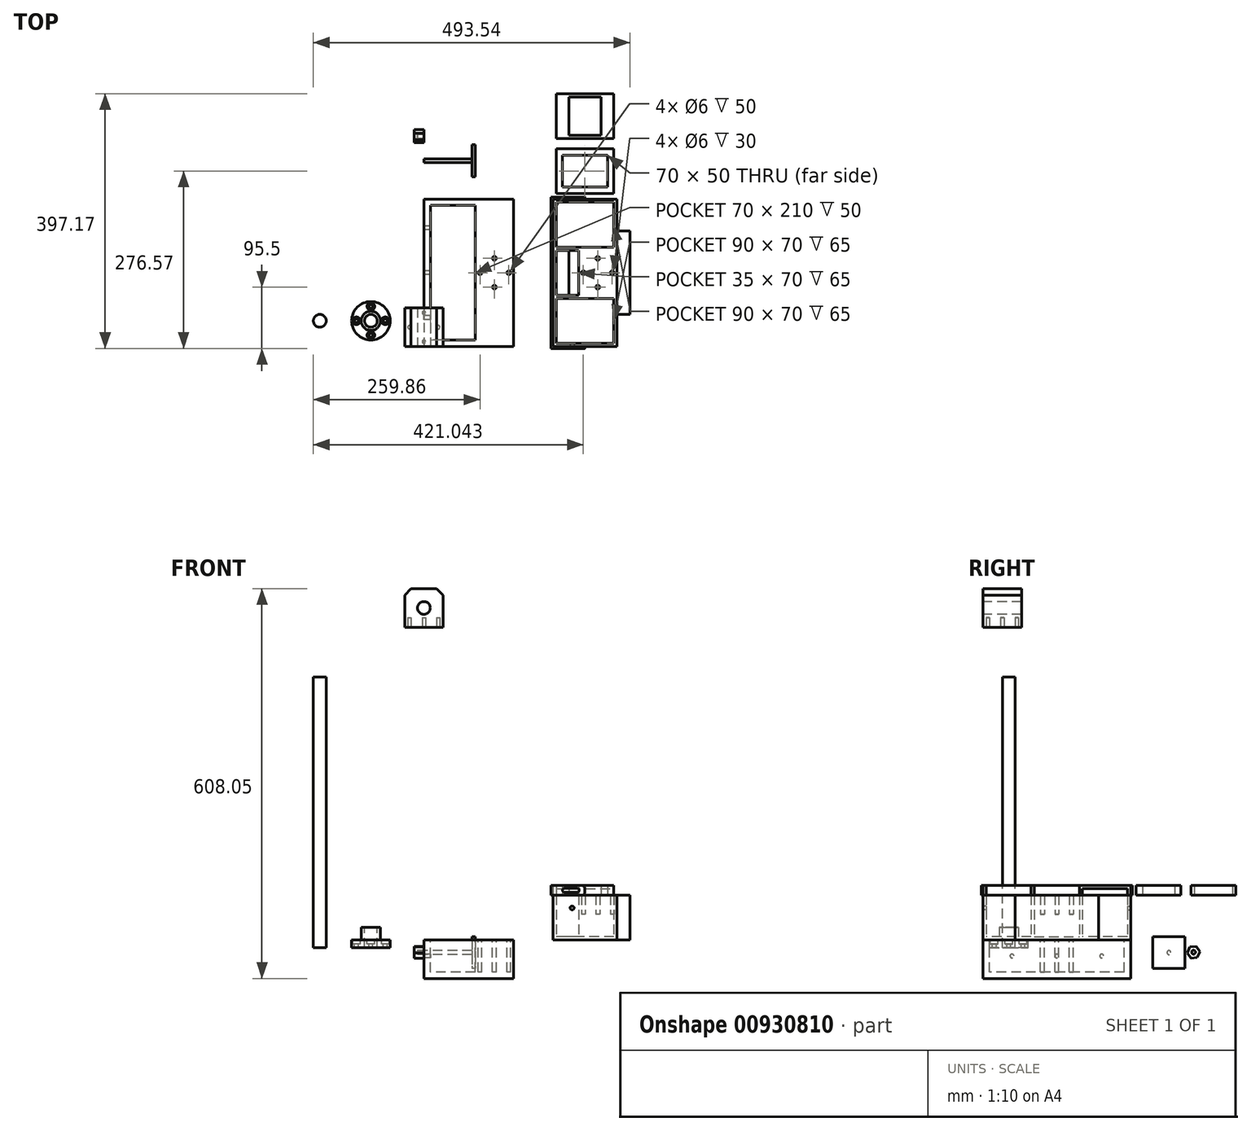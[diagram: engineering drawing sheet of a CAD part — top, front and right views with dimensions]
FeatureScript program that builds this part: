
annotation { "Feature Type Name" : "Feature", "Feature Type Description" : "" }
export const myFeature = defineFeature(function(context is Context, id is Id, definition is map)
    precondition{}
    {
        {
            var Q0;
            Q0=qCreatedBy(makeId("Front.planeOp"),FACE);
            var sketch = newSketch(context, id + "F0", { "sketchPlane" : qUnion([Q0])});
            skLineSegment(sketch, "E0.bottom", {"start": v(0, -100) * mm, "end": v(140, -100) * mm});
            skLineSegment(sketch, "E0.top", {"start": v(0, -160) * mm, "end": v(140, -160) * mm});
            skLineSegment(sketch, "E0.left", {"start": v(0, -100) * mm, "end": v(0, -160) * mm});
            skLineSegment(sketch, "E0.right", {"start": v(140, -100) * mm, "end": v(140, -160) * mm});
            skSolve(sketch);
        }
        {
            var Q0;
            Q0=qSketchRegion(id+"F0",true);
            extrude(context, id + "F1", {"entities" : qUnion([Q0]), "oppositeDirection" : true, "depth" : 230 * mm, "offsetDistance" : 25 * mm});
        }
        {
            var Q0;
            Q0=makeQuery(id+"F1.opExtrude","SWEPT_FACE",FACE,{"disambiguationData":[OSD([sQuery(id+"F0.wireOp",EDGE,"E0.bottom")])]});
            var sketch = newSketch(context, id + "F2", { "sketchPlane" : qUnion([Q0])});
            skCircle(sketch, "E1", {"center": v(-82.66, 40) * mm, "radius": 30 * mm});
            skCircle(sketch, "E2", {"center": v(-82.66, 40) * mm, "radius": 10 * mm});
            skCircle(sketch, "E3", {"center": v(-82.66, 40) * mm, "radius": 15 * mm});
            skCircle(sketch, "E4", {"center": v(-82.66, 62.5) * mm, "radius": 3 * mm});
            skCircle(sketch, "E5.1.0", {"center": v(-105.16, 40) * mm, "radius": 3 * mm});
            skCircle(sketch, "E5.2.0", {"center": v(-82.66, 17.5) * mm, "radius": 3 * mm});
            skCircle(sketch, "E5.3.0", {"center": v(-60.16, 40) * mm, "radius": 3 * mm});
            skCircle(sketch, "E6", {"center": v(-82.66, 62.5) * mm, "radius": 6 * mm});
            skCircle(sketch, "E7", {"center": v(-60.16, 40) * mm, "radius": 6 * mm});
            skCircle(sketch, "E8", {"center": v(-82.66, 17.5) * mm, "radius": 6 * mm});
            skCircle(sketch, "E9", {"center": v(-105.16, 40) * mm, "radius": 6 * mm});
            skCircle(sketch, "E10", {"center": v(-162.36, 40) * mm, "radius": 10 * mm});
            skSolve(sketch);
        }
        {
            var Q0;
            Q0=makeQuery(id+"F2.imprint","IMPRINT",FACE,{"disambiguationData":[TD([[makeQuery(id+"F2.imprint","IMPRINT",EDGE,{"derivedFrom":sQuery(id+"F2.wireOp",EDGE,"E1")}),1.0]])]});
            var Q1;
            Q1=makeQuery(id+"F2.imprint","IMPRINT",FACE,{"disambiguationData":[TD([[makeQuery(id+"F2.imprint","IMPRINT",EDGE,{"derivedFrom":sQuery(id+"F2.wireOp",EDGE,"E5.1.0")}),-1.0]])]});
            var Q2;
            Q2=makeQuery(id+"F2.imprint","IMPRINT",FACE,{"disambiguationData":[TD([[makeQuery(id+"F2.imprint","IMPRINT",EDGE,{"derivedFrom":sQuery(id+"F2.wireOp",EDGE,"E2")}),-1.0]])]});
            var Q3;
            Q3=makeQuery(id+"F2.imprint","IMPRINT",FACE,{"disambiguationData":[TD([[makeQuery(id+"F2.imprint","IMPRINT",EDGE,{"derivedFrom":sQuery(id+"F2.wireOp",EDGE,"E4")}),-1.0]])]});
            var Q4;
            Q4=makeQuery(id+"F2.imprint","IMPRINT",FACE,{"disambiguationData":[TD([[makeQuery(id+"F2.imprint","IMPRINT",EDGE,{"derivedFrom":sQuery(id+"F2.wireOp",EDGE,"E5.3.0")}),-1.0]])]});
            var Q5;
            Q5=makeQuery(id+"F2.imprint","IMPRINT",FACE,{"disambiguationData":[TD([[makeQuery(id+"F2.imprint","IMPRINT",EDGE,{"derivedFrom":sQuery(id+"F2.wireOp",EDGE,"E5.2.0")}),-1.0]])]});
            var Q6;
            Q6=makeQuery(id+"F2.imprint","IMPRINT",FACE,{"disambiguationData":[TD([[makeQuery(id+"F2.imprint","IMPRINT",EDGE,{"derivedFrom":sQuery(id+"F2.wireOp",EDGE,"E1")}),1.0]])]});
            var Q7;
            Q7=makeQuery(id+"F2.imprint","IMPRINT",FACE,{"disambiguationData":[TD([[makeQuery(id+"F2.imprint","IMPRINT",EDGE,{"derivedFrom":sQuery(id+"F2.wireOp",EDGE,"E10")}),1.0]])]});
            extrude(context, id + "F3", {"entities" : qUnion([Q0, Q1, Q2, Q3, Q4, Q5, Q6, Q7]), "oppositeDirection" : true, "depth" : 12 * mm, "offsetDistance" : 25 * mm});
        }
        {
            var Q0;
            Q0=makeQuery(id+"F2.imprint","IMPRINT",FACE,{"disambiguationData":[TD([[makeQuery(id+"F2.imprint","IMPRINT",EDGE,{"derivedFrom":sQuery(id+"F2.wireOp",EDGE,"E4")}),-1.0]])]});
            var Q1;
            Q1=makeQuery(id+"F2.imprint","IMPRINT",FACE,{"disambiguationData":[TD([[makeQuery(id+"F2.imprint","IMPRINT",EDGE,{"derivedFrom":sQuery(id+"F2.wireOp",EDGE,"E5.3.0")}),-1.0]])]});
            var Q2;
            Q2=makeQuery(id+"F2.imprint","IMPRINT",FACE,{"disambiguationData":[TD([[makeQuery(id+"F2.imprint","IMPRINT",EDGE,{"derivedFrom":sQuery(id+"F2.wireOp",EDGE,"E5.2.0")}),-1.0]])]});
            var Q3;
            Q3=makeQuery(id+"F2.imprint","IMPRINT",FACE,{"disambiguationData":[TD([[makeQuery(id+"F2.imprint","IMPRINT",EDGE,{"derivedFrom":sQuery(id+"F2.wireOp",EDGE,"E5.1.0")}),-1.0]])]});
            extrude(context, id + "F4", {"entities" : qUnion([Q0, Q1, Q2, Q3]), "operationType" : NewBodyOperationType.REMOVE, "oppositeDirection" : true, "depth" : 6 * mm, "offsetDistance" : 25 * mm});
        }
        {
            var Q0;
            Q0=makeQuery(id+"F2.imprint","IMPRINT",FACE,{"disambiguationData":[TD([[makeQuery(id+"F2.imprint","IMPRINT",EDGE,{"derivedFrom":sQuery(id+"F2.wireOp",EDGE,"E2")}),-1.0]])]});
            extrude(context, id + "F5", {"entities" : qUnion([Q0]), "operationType" : NewBodyOperationType.ADD, "depth" : 20 * mm, "offsetDistance" : 25 * mm});
        }
        {
            var Q0;
            Q0=makeQuery(id+"F2.imprint","IMPRINT",FACE,{"disambiguationData":[TD([[makeQuery(id+"F2.imprint","IMPRINT",EDGE,{"derivedFrom":sQuery(id+"F2.wireOp",EDGE,"E10")}),1.0]])]});
            extrude(context, id + "F6", {"entities" : qUnion([Q0]), "operationType" : NewBodyOperationType.ADD, "depth" : 410 * mm, "offsetDistance" : 25 * mm});
        }
        {
            var Q0;
            Q0=qCreatedBy(makeId("Front.planeOp"),FACE);
            var sketch = newSketch(context, id + "F7", { "sketchPlane" : qUnion([Q0])});
            skLineSegment(sketch, "E11.top", {"start": v(-30, 388.05) * mm, "end": v(30, 388.05) * mm});
            skLineSegment(sketch, "E11.left", {"start": v(-30, 448.05) * mm, "end": v(-30, 388.05) * mm});
            skLineSegment(sketch, "E11.right", {"start": v(30, 448.05) * mm, "end": v(30, 388.05) * mm});
            skPoint(sketch, "E11.middle", {"position": v(0, 418.05) * mm});
            skCircle(sketch, "E12", {"center": v(0, 418.05) * mm, "radius": 10 * mm});
            skLineSegment(sketch, "E13", {"start": v(30, 448.05) * mm, "end": v(-30, 448.05) * mm});
            skSolve(sketch);
        }
        {
            var Q0;
            Q0=qSketchRegion(id+"F7",true);
            extrude(context, id + "F8", {"entities" : qUnion([Q0]), "oppositeDirection" : true, "depth" : 60 * mm, "offsetDistance" : 25 * mm});
        }
        {
            var Q0;
            Q0=makeQuery(id+"F8.opExtrude","SWEPT_FACE",FACE,{"disambiguationData":[OSD([sQuery(id+"F7.wireOp",EDGE,"E11.top")])]});
            var sketch = newSketch(context, id + "F9", { "sketchPlane" : qUnion([Q0])});
            skCircle(sketch, "E14", {"center": v(0, -7.5) * mm, "radius": 2.6 * mm});
            skCircle(sketch, "E15.1.0", {"center": v(-22.5, -30) * mm, "radius": 2.6 * mm});
            skCircle(sketch, "E15.2.0", {"center": v(0, -52.5) * mm, "radius": 2.6 * mm});
            skCircle(sketch, "E15.3.0", {"center": v(22.5, -30) * mm, "radius": 2.6 * mm});
            skPoint(sketch, "E15.center", {"position": v(0, -30) * mm});
            skSolve(sketch);
        }
        {
            var Q0;
            Q0=qSketchRegion(id+"F9",true);
            extrude(context, id + "F10", {"entities" : qUnion([Q0]), "operationType" : NewBodyOperationType.REMOVE, "oppositeDirection" : true, "depth" : 15 * mm, "offsetDistance" : 25 * mm});
        }
        {
            var Q0;
            {var subQ0=sQuery(id+"F0.wireOp",EDGE,"E0.bottom");Q0=makeQuery(id+"F2.imprint","IMPRINT",FACE,{"disambiguationData":[TD([[makeQuery(id+"F2.imprint","IMPRINT",EDGE,{"derivedFrom":makeQuery(id+"F1.opExtrude","CAP_EDGE",EDGE,{"disambiguationData":[OSD([subQ0])],"isStart":true})}),1.0]])]});}
            var sketch = newSketch(context, id + "F11", { "sketchPlane" : qUnion([Q0])});
            skLineSegment(sketch, "E16.bottom", {"start": v(80, 220) * mm, "end": v(10, 220) * mm});
            skLineSegment(sketch, "E16.top", {"start": v(80, 10) * mm, "end": v(10, 10) * mm});
            skLineSegment(sketch, "E16.left", {"start": v(80, 220) * mm, "end": v(80, 10) * mm});
            skLineSegment(sketch, "E16.right", {"start": v(10, 220) * mm, "end": v(10, 10) * mm});
            skCircle(sketch, "E17", {"center": v(110, 137.5) * mm, "radius": 3 * mm});
            skCircle(sketch, "E18.1.0", {"center": v(87.5, 115) * mm, "radius": 3 * mm});
            skCircle(sketch, "E18.2.0", {"center": v(110, 92.5) * mm, "radius": 3 * mm});
            skPoint(sketch, "E18.center", {"position": v(110, 115) * mm});
            skCircle(sketch, "E19.1.3.0", {"center": v(132.5, 115) * mm, "radius": 3 * mm});
            skSolve(sketch);
        }
        {
            var Q0;
            Q0 = qSketchRegion(id + "F11", true);
            extrude(context, id + "F12", {"entities" : qUnion([Q0]), "operationType" : NewBodyOperationType.REMOVE, "oppositeDirection" : true, "depth" : 50 * mm, "offsetDistance" : 25 * mm});
        }
        {
            var Q0;
            Q0=makeQuery(id+"F1.opExtrude","SWEPT_FACE",FACE,{"disambiguationData":[OSD([sQuery(id+"F0.wireOp",EDGE,"E0.left")])]});
            var sketch = newSketch(context, id + "F13", { "sketchPlane" : qUnion([Q0])});
            skCircle(sketch, "E20", {"center": v(-115, -125) * mm, "radius": 3 * mm});
            skCircle(sketch, "E21", {"center": v(-185, -125) * mm, "radius": 3 * mm});
            skCircle(sketch, "E22.MirrorC", {"center": v(-45, -125) * mm, "radius": 3 * mm});
            skSolve(sketch);
        }
        {
            var Q0;
            Q0 = qSketchRegion(id + "F13", true);
            extrude(context, id + "F14", {"entities" : qUnion([Q0]), "operationType" : NewBodyOperationType.REMOVE, "oppositeDirection" : true, "depth" : 10 * mm, "offsetDistance" : 25 * mm});
        }
        {
            var Q0;
            Q0=makeQuery(id+"F1.opExtrude","SWEPT_FACE",FACE,{"disambiguationData":[OSD([sQuery(id+"F0.wireOp",EDGE,"E0.left")])]});
            var sketch = newSketch(context, id + "F15", { "sketchPlane" : qUnion([Q0])});
            skLineSegment(sketch, "E23.bottom", {"start": v(-314.84, -94.64) * mm, "end": v(-264.84, -94.64) * mm});
            skLineSegment(sketch, "E23.top", {"start": v(-314.84, -144.64) * mm, "end": v(-264.84, -144.64) * mm});
            skLineSegment(sketch, "E23.left", {"start": v(-314.84, -94.64) * mm, "end": v(-314.84, -144.64) * mm});
            skLineSegment(sketch, "E23.right", {"start": v(-264.84, -94.64) * mm, "end": v(-264.84, -144.64) * mm});
            skPoint(sketch, "E23.middle", {"position": v(-289.84, -119.64) * mm});
            skCircle(sketch, "E24", {"center": v(-289.84, -119.64) * mm, "radius": 3 * mm});
            skSolve(sketch);
        }
        {
            var Q0;
            Q0=makeQuery(id+"F1.opExtrude","SWEPT_FACE",FACE,{"disambiguationData":[OSD([sQuery(id+"F0.wireOp",EDGE,"E0.left")])]});
            var sketch = newSketch(context, id + "F16", { "sketchPlane" : qUnion([Q0])});
            skCircle(sketch, "E25", {"center": v(-328.25, -119.07) * mm, "radius": 3 * mm});
            skCircle(sketch, "E26.cCircle", {"center": v(-328.25, -119.07) * mm, "radius": 10 * mm, "construction": true});
            skLineSegment(sketch, "E26.0", {"start": v(-322.4, -110.95) * mm, "end": v(-318.3, -120.07) * mm});
            skLineSegment(sketch, "E26.1", {"start": v(-318.3, -120.07) * mm, "end": v(-324.15, -128.18) * mm});
            skLineSegment(sketch, "E26.2", {"start": v(-324.15, -128.18) * mm, "end": v(-334.1, -127.18) * mm});
            skLineSegment(sketch, "E26.3", {"start": v(-334.1, -127.18) * mm, "end": v(-338.2, -118.06) * mm});
            skLineSegment(sketch, "E26.4", {"start": v(-338.2, -118.06) * mm, "end": v(-332.36, -109.95) * mm});
            skLineSegment(sketch, "E26.5", {"start": v(-332.36, -109.95) * mm, "end": v(-322.4, -110.95) * mm});
            skSolve(sketch);
        }
        {
            var Q0;
            Q0=makeQuery(id+"F16.imprint","IMPRINT",FACE,{"disambiguationData":[TD([[makeQuery(id+"F16.imprint","IMPRINT",EDGE,{"derivedFrom":sQuery(id+"F16.wireOp",EDGE,"E25")}),-1.0]])]});
            var Q1;
            Q1=makeQuery(id+"F16.imprint","IMPRINT",FACE,{"disambiguationData":[TD([[makeQuery(id+"F16.imprint","IMPRINT",EDGE,{"derivedFrom":sQuery(id+"F16.wireOp",EDGE,"E25")}),1.0]])]});
            extrude(context, id + "F17", {"entities" : qUnion([Q0, Q1]), "depth" : 15 * mm, "offsetDistance" : 25 * mm});
        }
        {
            var Q0;
            Q0=makeQuery(id+"F16.imprint","IMPRINT",FACE,{"disambiguationData":[TD([[makeQuery(id+"F16.imprint","IMPRINT",EDGE,{"derivedFrom":sQuery(id+"F16.wireOp",EDGE,"E25")}),1.0]])]});
            extrude(context, id + "F18", {"entities" : qUnion([Q0]), "operationType" : NewBodyOperationType.REMOVE, "depth" : 10 * mm, "offsetDistance" : 25 * mm});
        }
        {
            var Q0;
            Q0=makeQuery(id+"F15.imprint","IMPRINT",FACE,{"disambiguationData":[TD([[makeQuery(id+"F15.imprint","IMPRINT",EDGE,{"derivedFrom":sQuery(id+"F15.wireOp",EDGE,"E23.bottom")}),-1.0]])]});
            var Q1;
            Q1=makeQuery(id+"F15.imprint","IMPRINT",FACE,{"disambiguationData":[TD([[makeQuery(id+"F15.imprint","IMPRINT",EDGE,{"derivedFrom":sQuery(id+"F15.wireOp",EDGE,"E24")}),1.0]])]});
            extrude(context, id + "F19", {"entities" : qUnion([Q0, Q1]), "oppositeDirection" : true, "depth" : 80 * mm, "offsetDistance" : 25 * mm});
        }
        {
            var Q0;
            Q0 = qSketchRegion(id + "F15", true);
            extrude(context, id + "F20", {"entities" : qUnion([Q0]), "operationType" : NewBodyOperationType.REMOVE, "oppositeDirection" : true, "depth" : 75 * mm, "offsetDistance" : 25 * mm});
        }
        {
            var Q0;
            Q0=makeQuery(id+"F8.opExtrude","SWEPT_EDGE",EDGE,{"disambiguationData":[OSD([sQuery(id+"F7.wireOp",EDGE,"E11.left"),sQuery(id+"F7.wireOp",EDGE,"E13")])]});
            var Q1;
            Q1=makeQuery(id+"F8.opExtrude","SWEPT_EDGE",EDGE,{"disambiguationData":[OSD([sQuery(id+"F7.wireOp",EDGE,"E11.right"),sQuery(id+"F7.wireOp",EDGE,"E13")])]});
            chamfer(context, id + "F21", {"entities" : qUnion([Q0, Q1]), "width" : 10 * mm, "tangentPropagation" : true});
        }
        {
            var Q0;
            {var subQ0=sQuery(id+"F0.wireOp",EDGE,"E0.bottom");Q0=makeQuery(id+"F2.imprint","IMPRINT",FACE,{"disambiguationData":[TD([[makeQuery(id+"F2.imprint","IMPRINT",EDGE,{"derivedFrom":makeQuery(id+"F1.opExtrude","CAP_EDGE",EDGE,{"disambiguationData":[OSD([subQ0])],"isStart":true})}),1.0]])]});}
            var sketch = newSketch(context, id + "F22", { "sketchPlane" : qUnion([Q0])});
            skLineSegment(sketch, "E27.bottom", {"start": v(201.18, 0) * mm, "end": v(301.18, 0) * mm});
            skLineSegment(sketch, "E27.top", {"start": v(201.18, 230) * mm, "end": v(301.18, 230) * mm});
            skLineSegment(sketch, "E27.left", {"start": v(201.18, 0) * mm, "end": v(201.18, 230) * mm});
            skLineSegment(sketch, "E27.right", {"start": v(301.18, 0) * mm, "end": v(301.18, 230) * mm});
            skLineSegment(sketch, "E28.0", {"start": v(206.18, 225) * mm, "end": v(296.18, 225) * mm});
            skLineSegment(sketch, "E28.1", {"start": v(206.18, 5) * mm, "end": v(206.18, 75) * mm});
            skLineSegment(sketch, "E28.2", {"start": v(206.18, 5) * mm, "end": v(296.18, 5) * mm});
            skLineSegment(sketch, "E28.3", {"start": v(296.18, 5) * mm, "end": v(296.18, 75) * mm});
            skLineSegment(sketch, "E29", {"start": v(206.18, 75) * mm, "end": v(296.18, 75) * mm});
            skLineSegment(sketch, "E30", {"start": v(206.18, 155) * mm, "end": v(296.18, 155) * mm});
            skLineSegment(sketch, "E31.trimOffspring", {"start": v(206.18, 155) * mm, "end": v(206.18, 225) * mm});
            skLineSegment(sketch, "E32.trimOffspring", {"start": v(296.18, 155) * mm, "end": v(296.18, 225) * mm});
            skCircle(sketch, "E33", {"center": v(271.18, 137.5) * mm, "radius": 3 * mm});
            skCircle(sketch, "E34", {"center": v(271.18, 92.5) * mm, "radius": 3 * mm});
            skCircle(sketch, "E35", {"center": v(293.68, 115) * mm, "radius": 3 * mm});
            skCircle(sketch, "E36", {"center": v(248.68, 115) * mm, "radius": 3 * mm});
            skLineSegment(sketch, "E37.bottom", {"start": v(206.18, 150) * mm, "end": v(241.18, 150) * mm});
            skLineSegment(sketch, "E37.top", {"start": v(206.18, 80) * mm, "end": v(241.18, 80) * mm});
            skLineSegment(sketch, "E37.left", {"start": v(206.18, 150) * mm, "end": v(206.18, 80) * mm});
            skLineSegment(sketch, "E37.right", {"start": v(241.18, 150) * mm, "end": v(241.18, 80) * mm});
            skSolve(sketch);
        }
        {
            var Q0;
            Q0=makeQuery(id+"F22.imprint","IMPRINT",FACE,{"disambiguationData":[TD([[makeQuery(id+"F22.imprint","IMPRINT",EDGE,{"derivedFrom":sQuery(id+"F22.wireOp",EDGE,"E27.bottom")}),1.0]])]});
            var Q1;
            Q1=makeQuery(id+"F22.imprint","IMPRINT",FACE,{"disambiguationData":[TD([[makeQuery(id+"F22.imprint","IMPRINT",EDGE,{"derivedFrom":sQuery(id+"F22.wireOp",EDGE,"E34")}),1.0]])]});
            var Q2;
            Q2=makeQuery(id+"F22.imprint","IMPRINT",FACE,{"disambiguationData":[TD([[makeQuery(id+"F22.imprint","IMPRINT",EDGE,{"derivedFrom":sQuery(id+"F22.wireOp",EDGE,"E36")}),1.0]])]});
            var Q3;
            Q3=makeQuery(id+"F22.imprint","IMPRINT",FACE,{"disambiguationData":[TD([[makeQuery(id+"F22.imprint","IMPRINT",EDGE,{"derivedFrom":sQuery(id+"F22.wireOp",EDGE,"E35")}),1.0]])]});
            var Q4;
            Q4=makeQuery(id+"F22.imprint","IMPRINT",FACE,{"disambiguationData":[TD([[makeQuery(id+"F22.imprint","IMPRINT",EDGE,{"derivedFrom":sQuery(id+"F22.wireOp",EDGE,"E33")}),1.0]])]});
            var Q5;
            Q5=makeQuery(id+"F22.imprint","IMPRINT",FACE,{"disambiguationData":[TD([[makeQuery(id+"F22.imprint","IMPRINT",EDGE,{"derivedFrom":sQuery(id+"F22.wireOp",EDGE,"E37.bottom")}),-1.0]])]});
            var Q6;
            Q6=makeQuery(id+"F22.imprint","IMPRINT",FACE,{"disambiguationData":[TD([[makeQuery(id+"F22.imprint","IMPRINT",EDGE,{"derivedFrom":sQuery(id+"F22.wireOp",EDGE,"E28.1")}),-1.0]])]});
            var Q7;
            Q7=makeQuery(id+"F22.imprint","IMPRINT",FACE,{"disambiguationData":[TD([[makeQuery(id+"F22.imprint","IMPRINT",EDGE,{"derivedFrom":sQuery(id+"F22.wireOp",EDGE,"E28.0")}),-1.0]])]});
            extrude(context, id + "F23", {"entities" : qUnion([Q0, Q1, Q2, Q3, Q4, Q5, Q6, Q7]), "depth" : 5 * mm, "offsetDistance" : 25 * mm});
        }
        {
            var Q0;
            Q0 = qSketchRegion(id + "F22", true);
            extrude(context, id + "F24", {"entities" : qUnion([Q0]), "operationType" : NewBodyOperationType.ADD, "depth" : 70 * mm, "offsetDistance" : 25 * mm});
        }
        {
            var Q0;
            Q0=makeQuery(id+"F22.imprint","IMPRINT",FACE,{"disambiguationData":[TD([[makeQuery(id+"F22.imprint","IMPRINT",EDGE,{"derivedFrom":sQuery(id+"F22.wireOp",EDGE,"E36")}),1.0]])]});
            var Q1;
            Q1=makeQuery(id+"F22.imprint","IMPRINT",FACE,{"disambiguationData":[TD([[makeQuery(id+"F22.imprint","IMPRINT",EDGE,{"derivedFrom":sQuery(id+"F22.wireOp",EDGE,"E33")}),1.0]])]});
            var Q2;
            Q2=makeQuery(id+"F22.imprint","IMPRINT",FACE,{"disambiguationData":[TD([[makeQuery(id+"F22.imprint","IMPRINT",EDGE,{"derivedFrom":sQuery(id+"F22.wireOp",EDGE,"E34")}),1.0]])]});
            var Q3;
            Q3=makeQuery(id+"F22.imprint","IMPRINT",FACE,{"disambiguationData":[TD([[makeQuery(id+"F22.imprint","IMPRINT",EDGE,{"derivedFrom":sQuery(id+"F22.wireOp",EDGE,"E35")}),1.0]])]});
            extrude(context, id + "F25", {"entities" : qUnion([Q0, Q1, Q2, Q3]), "operationType" : NewBodyOperationType.ADD, "depth" : 40 * mm, "offsetDistance" : 25 * mm});
        }
        {
            var Q0;
            {var subQ0=sQuery(id+"F22.wireOp",EDGE,"E27.right");Q0=makeQuery(id+"F24.boolean.opBoolean","MERGE",FACE,{"derivedFrom":[makeQuery(id+"F23.opExtrude","SWEPT_FACE",FACE,{"disambiguationData":[OSD([subQ0])]}),makeQuery(id+"F24.opExtrude","SWEPT_FACE",FACE,{"disambiguationData":[OSD([subQ0])]})]});}
            var sketch = newSketch(context, id + "F26", { "sketchPlane" : qUnion([Q0])});
            skLineSegment(sketch, "E38.bottom", {"start": v(180, -30) * mm, "end": v(50, -30) * mm});
            skLineSegment(sketch, "E38.top", {"start": v(180, -100) * mm, "end": v(50, -100) * mm});
            skLineSegment(sketch, "E38.left", {"start": v(180, -30) * mm, "end": v(180, -100) * mm});
            skLineSegment(sketch, "E39", {"start": v(50, -30) * mm, "end": v(50, -100) * mm});
            skSolve(sketch);
        }
        {
            var Q0;
            Q0 = qSketchRegion(id + "F26", true);
            extrude(context, id + "F27", {"entities" : qUnion([Q0]), "depth" : 20 * mm, "offsetDistance" : 25 * mm});
        }
        {
            var Q0;
            Q0=makeQuery(id+"F24.opExtrude","CAP_FACE",FACE,{"disambiguationData":[OSD([sQuery(id+"F22.wireOp",EDGE,"E27.bottom"),sQuery(id+"F22.wireOp",EDGE,"E27.top"),sQuery(id+"F22.wireOp",EDGE,"E27.left"),sQuery(id+"F22.wireOp",EDGE,"E27.right"),sQuery(id+"F22.wireOp",EDGE,"E28.0"),sQuery(id+"F22.wireOp",EDGE,"E28.1"),sQuery(id+"F22.wireOp",EDGE,"E28.2"),sQuery(id+"F22.wireOp",EDGE,"E28.3"),sQuery(id+"F22.wireOp",EDGE,"E29"),sQuery(id+"F22.wireOp",EDGE,"E30"),sQuery(id+"F22.wireOp",EDGE,"E31.trimOffspring"),sQuery(id+"F22.wireOp",EDGE,"E32.trimOffspring"),sQuery(id+"F22.wireOp",EDGE,"E33"),sQuery(id+"F22.wireOp",EDGE,"E34"),sQuery(id+"F22.wireOp",EDGE,"E35"),sQuery(id+"F22.wireOp",EDGE,"E36"),sQuery(id+"F22.wireOp",EDGE,"E37.bottom"),sQuery(id+"F22.wireOp",EDGE,"E37.top"),sQuery(id+"F22.wireOp",EDGE,"E37.left"),sQuery(id+"F22.wireOp",EDGE,"E37.right")])],"isStart":false});
            var sketch = newSketch(context, id + "F28", { "sketchPlane" : qUnion([Q0])});
            skLineSegment(sketch, "E40", {"start": v(251.18, 230) * mm, "end": v(251.18, 233) * mm});
            skLineSegment(sketch, "E41", {"start": v(251.18, 233) * mm, "end": v(198.18, 233) * mm});
            skLineSegment(sketch, "E42", {"start": v(198.18, 233) * mm, "end": v(198.18, -3) * mm});
            skLineSegment(sketch, "E43", {"start": v(198.18, -3) * mm, "end": v(251.18, -3) * mm});
            skLineSegment(sketch, "E44", {"start": v(251.18, 230) * mm, "end": v(201.18, 230) * mm});
            skLineSegment(sketch, "E45", {"start": v(201.18, 230) * mm, "end": v(201.18, 0) * mm});
            skLineSegment(sketch, "E46", {"start": v(201.18, 0) * mm, "end": v(251.18, 0) * mm});
            skLineSegment(sketch, "E47", {"start": v(251.18, 0) * mm, "end": v(251.18, -3) * mm});
            skSolve(sketch);
        }
        {
            var Q0;
            Q0 = qSketchRegion(id + "F28", true);
            extrude(context, id + "F29", {"entities" : qUnion([Q0]), "depth" : 15 * mm, "offsetDistance" : 25 * mm});
        }
        {
            var Q0;
            Q0=makeQuery(id+"F29.opExtrude","CAP_EDGE",EDGE,{"disambiguationData":[OSD([sQuery(id+"F28.wireOp",EDGE,"E47")])],"isStart":false});
            var Q1;
            Q1=makeQuery(id+"F29.opExtrude","CAP_EDGE",EDGE,{"disambiguationData":[OSD([sQuery(id+"F28.wireOp",EDGE,"E47")])],"isStart":true});
            var Q2;
            Q2=makeQuery(id+"F29.opExtrude","CAP_EDGE",EDGE,{"disambiguationData":[OSD([sQuery(id+"F28.wireOp",EDGE,"E40")])],"isStart":false});
            var Q3;
            Q3=makeQuery(id+"F29.opExtrude","CAP_EDGE",EDGE,{"disambiguationData":[OSD([sQuery(id+"F28.wireOp",EDGE,"E40")])],"isStart":true});
            fillet(context, id + "F30", {"entities" : qUnion([Q0, Q1, Q2, Q3]), "radius" : 5 * mm, "tangentPropagation" : true, "allowEdgeOverflow" : false});
        }
        {
            var Q0;
            Q0=makeQuery(id+"F29.opExtrude","SWEPT_FACE",FACE,{"disambiguationData":[OSD([sQuery(id+"F28.wireOp",EDGE,"E43")])]});
            var sketch = newSketch(context, id + "F31", { "sketchPlane" : qUnion([Q0])});
            skLineSegment(sketch, "E48.bottom", {"start": v(219.2, -19.5) * mm, "end": v(239.2, -19.5) * mm});
            skLineSegment(sketch, "E48.top", {"start": v(219.2, -25.5) * mm, "end": v(239.2, -25.5) * mm});
            skPoint(sketch, "E48.middle", {"position": v(229.2, -22.5) * mm});
            skPoint(sketch, "E48.middle.positionSnap0", {"position": v(251.18, -22.5) * mm});
            skPoint(sketch, "E48.centerSnap0", {"position": v(251.18, -22.5) * mm});
            skArc(sketch, "E49", {"start": v(219.2, -19.5) * mm, "mid": v(216.2, -22.5) * mm, "end": v(219.2, -25.5) * mm});
            skArc(sketch, "E50", {"start": v(239.2, -25.5) * mm, "mid": v(242.2, -22.5) * mm, "end": v(239.2, -19.5) * mm});
            skSolve(sketch);
        }
        {
            var Q0;
            Q0 = qSketchRegion(id + "F31", true);
            extrude(context, id + "F32", {"entities" : qUnion([Q0]), "operationType" : NewBodyOperationType.REMOVE, "endBound" : BoundingType.THROUGH_ALL, "oppositeDirection" : true, "depth" : 25 * mm, "offsetDistance" : 25 * mm});
        }
        {
            var Q0;
            {var subQ0=sQuery(id+"F22.wireOp",EDGE,"E27.bottom");Q0=makeQuery(id+"F24.boolean.opBoolean","MERGE",FACE,{"derivedFrom":[makeQuery(id+"F23.opExtrude","SWEPT_FACE",FACE,{"disambiguationData":[OSD([subQ0])]}),makeQuery(id+"F24.opExtrude","SWEPT_FACE",FACE,{"disambiguationData":[OSD([subQ0])]})]});}
            var sketch = newSketch(context, id + "F33", { "sketchPlane" : qUnion([Q0])});
            skCircle(sketch, "E51", {"center": v(231.18, -50) * mm, "radius": 3 * mm});
            skSolve(sketch);
        }
        {
            var Q0;
            Q0 = qSketchRegion(id + "F33", true);
            extrude(context, id + "F34", {"entities" : qUnion([Q0]), "operationType" : NewBodyOperationType.REMOVE, "endBound" : BoundingType.UP_TO_NEXT, "oppositeDirection" : true, "depth" : 25 * mm, "offsetDistance" : 25 * mm});
        }
        {
            var Q0;
            {var subQ0=sQuery(id+"F22.wireOp",EDGE,"E27.top");Q0=makeQuery(id+"F24.boolean.opBoolean","MERGE",FACE,{"derivedFrom":[makeQuery(id+"F23.opExtrude","SWEPT_FACE",FACE,{"disambiguationData":[OSD([subQ0])]}),makeQuery(id+"F24.opExtrude","SWEPT_FACE",FACE,{"disambiguationData":[OSD([subQ0])]})]});}
            var sketch = newSketch(context, id + "F35", { "sketchPlane" : qUnion([Q0])});
            skCircle(sketch, "E52", {"center": v(-231.18, -50) * mm, "radius": 3 * mm});
            skSolve(sketch);
        }
        {
            var Q0;
            Q0 = qSketchRegion(id + "F35", true);
            extrude(context, id + "F36", {"entities" : qUnion([Q0]), "operationType" : NewBodyOperationType.REMOVE, "endBound" : BoundingType.UP_TO_NEXT, "oppositeDirection" : true, "depth" : 25 * mm, "offsetDistance" : 25 * mm});
        }
        {
            var Q0;
            Q0=makeQuery(id+"F24.opExtrude","CAP_FACE",FACE,{"disambiguationData":[OSD([sQuery(id+"F22.wireOp",EDGE,"E27.bottom"),sQuery(id+"F22.wireOp",EDGE,"E27.top"),sQuery(id+"F22.wireOp",EDGE,"E27.left"),sQuery(id+"F22.wireOp",EDGE,"E27.right"),sQuery(id+"F22.wireOp",EDGE,"E28.0"),sQuery(id+"F22.wireOp",EDGE,"E28.1"),sQuery(id+"F22.wireOp",EDGE,"E28.2"),sQuery(id+"F22.wireOp",EDGE,"E28.3"),sQuery(id+"F22.wireOp",EDGE,"E29"),sQuery(id+"F22.wireOp",EDGE,"E30"),sQuery(id+"F22.wireOp",EDGE,"E31.trimOffspring"),sQuery(id+"F22.wireOp",EDGE,"E32.trimOffspring"),sQuery(id+"F22.wireOp",EDGE,"E33"),sQuery(id+"F22.wireOp",EDGE,"E34"),sQuery(id+"F22.wireOp",EDGE,"E35"),sQuery(id+"F22.wireOp",EDGE,"E36"),sQuery(id+"F22.wireOp",EDGE,"E37.bottom"),sQuery(id+"F22.wireOp",EDGE,"E37.top"),sQuery(id+"F22.wireOp",EDGE,"E37.left"),sQuery(id+"F22.wireOp",EDGE,"E37.right")])],"isStart":false});
            var sketch = newSketch(context, id + "F37", { "sketchPlane" : qUnion([Q0])});
            skLineSegment(sketch, "E53.bottom", {"start": v(296.18, 75) * mm, "end": v(206.18, 75) * mm});
            skLineSegment(sketch, "E53.top", {"start": v(296.18, 5) * mm, "end": v(206.18, 5) * mm});
            skLineSegment(sketch, "E53.left", {"start": v(296.18, 75) * mm, "end": v(296.18, 5) * mm});
            skLineSegment(sketch, "E53.right", {"start": v(206.18, 75) * mm, "end": v(206.18, 5) * mm});
            skLineSegment(sketch, "E54.bottom", {"start": v(296.18, 225) * mm, "end": v(206.18, 225) * mm});
            skLineSegment(sketch, "E54.top", {"start": v(296.18, 155) * mm, "end": v(206.18, 155) * mm});
            skLineSegment(sketch, "E54.left", {"start": v(296.18, 225) * mm, "end": v(296.18, 155) * mm});
            skLineSegment(sketch, "E54.right", {"start": v(206.18, 225) * mm, "end": v(206.18, 155) * mm});
            skLineSegment(sketch, "E55.bottom", {"start": v(241.18, 150) * mm, "end": v(226.18, 150) * mm});
            skLineSegment(sketch, "E55.top", {"start": v(241.18, 80) * mm, "end": v(226.18, 80) * mm});
            skLineSegment(sketch, "E55.left", {"start": v(241.18, 150) * mm, "end": v(241.18, 80) * mm});
            skLineSegment(sketch, "E55.right", {"start": v(226.18, 150) * mm, "end": v(226.18, 80) * mm});
            skLineSegment(sketch, "E56.bottom", {"start": v(296.18, 238.57) * mm, "end": v(206.18, 238.57) * mm});
            skLineSegment(sketch, "E56.top", {"start": v(296.18, 308.57) * mm, "end": v(206.18, 308.57) * mm});
            skLineSegment(sketch, "E56.left", {"start": v(296.18, 238.57) * mm, "end": v(296.18, 308.57) * mm});
            skLineSegment(sketch, "E56.right", {"start": v(206.18, 238.57) * mm, "end": v(206.18, 308.57) * mm});
            skLineSegment(sketch, "E57.0", {"start": v(286.18, 298.57) * mm, "end": v(216.18, 298.57) * mm});
            skLineSegment(sketch, "E57.1", {"start": v(286.18, 248.57) * mm, "end": v(286.18, 298.57) * mm});
            skLineSegment(sketch, "E57.2", {"start": v(286.18, 248.57) * mm, "end": v(216.18, 248.57) * mm});
            skLineSegment(sketch, "E57.3", {"start": v(216.18, 248.57) * mm, "end": v(216.18, 298.57) * mm});
            skLineSegment(sketch, "E58.bottom", {"start": v(296.18, 324.17) * mm, "end": v(206.18, 324.17) * mm});
            skLineSegment(sketch, "E58.top", {"start": v(296.18, 394.17) * mm, "end": v(206.18, 394.17) * mm});
            skLineSegment(sketch, "E58.left", {"start": v(296.18, 324.17) * mm, "end": v(296.18, 394.17) * mm});
            skLineSegment(sketch, "E58.right", {"start": v(206.18, 324.17) * mm, "end": v(206.18, 394.17) * mm});
            skLineSegment(sketch, "E59.bottom", {"start": v(226.18, 389.17) * mm, "end": v(276.18, 389.17) * mm});
            skLineSegment(sketch, "E59.top", {"start": v(226.18, 329.17) * mm, "end": v(276.18, 329.17) * mm});
            skLineSegment(sketch, "E59.left", {"start": v(226.18, 389.17) * mm, "end": v(226.18, 329.17) * mm});
            skLineSegment(sketch, "E59.right", {"start": v(276.18, 389.17) * mm, "end": v(276.18, 329.17) * mm});
            skSolve(sketch);
        }
        {
            var Q0;
            Q0=makeQuery(id+"F37.imprint","IMPRINT",FACE,{"disambiguationData":[TD([[makeQuery(id+"F37.imprint","IMPRINT",EDGE,{"derivedFrom":sQuery(id+"F37.wireOp",EDGE,"E53.bottom")}),-1.0]])]});
            var Q1;
            Q1=makeQuery(id+"F37.imprint","IMPRINT",FACE,{"disambiguationData":[TD([[makeQuery(id+"F37.imprint","IMPRINT",EDGE,{"derivedFrom":sQuery(id+"F37.wireOp",EDGE,"E55.bottom")}),-1.0]])]});
            var Q2;
            Q2=makeQuery(id+"F37.imprint","IMPRINT",FACE,{"disambiguationData":[TD([[makeQuery(id+"F37.imprint","IMPRINT",EDGE,{"derivedFrom":sQuery(id+"F37.wireOp",EDGE,"E56.bottom")}),-1.0]])]});
            var Q3;
            Q3=makeQuery(id+"F37.imprint","IMPRINT",FACE,{"disambiguationData":[TD([[makeQuery(id+"F37.imprint","IMPRINT",EDGE,{"derivedFrom":sQuery(id+"F37.wireOp",EDGE,"E58.bottom")}),-1.0]])]});
            extrude(context, id + "F38", {"entities" : qUnion([Q0, Q1, Q2, Q3]), "depth" : 15 * mm, "offsetDistance" : 25 * mm});
        }
        {
            var Q0;
            Q0=makeQuery(id+"F37.imprint","IMPRINT",FACE,{"disambiguationData":[TD([[makeQuery(id+"F37.imprint","IMPRINT",EDGE,{"derivedFrom":sQuery(id+"F37.wireOp",EDGE,"E54.bottom")}),-1.0]])]});
            extrude(context, id + "F39", {"entities" : qUnion([Q0]), "depth" : 10 * mm, "offsetDistance" : 25 * mm});
        }
    });
